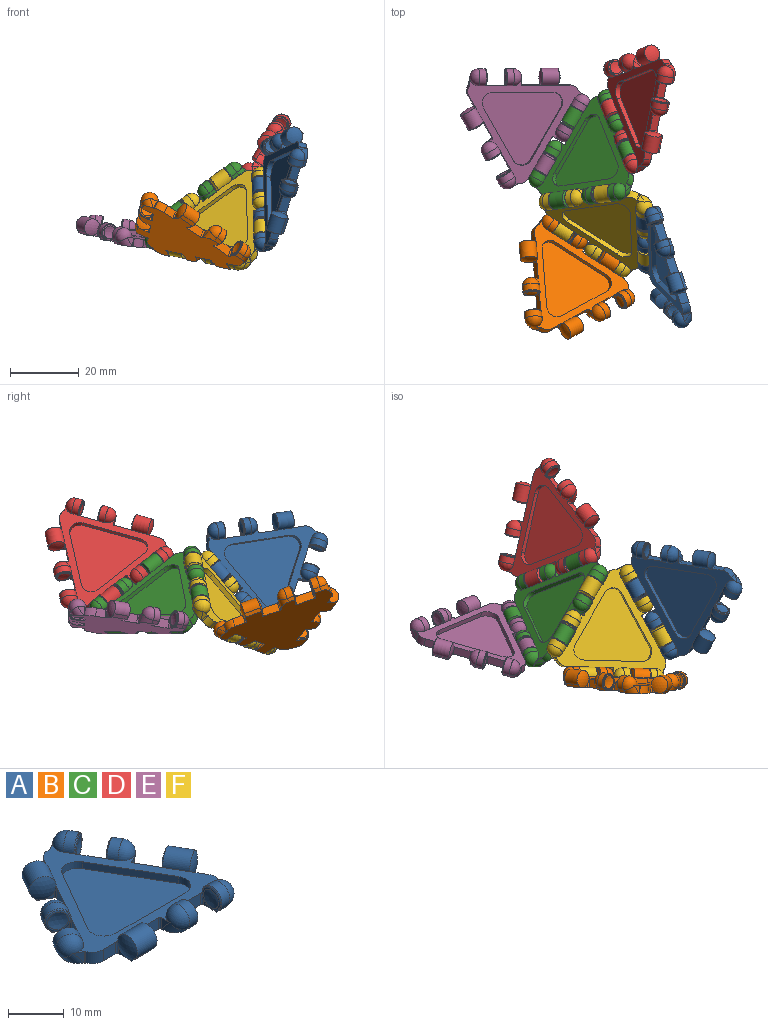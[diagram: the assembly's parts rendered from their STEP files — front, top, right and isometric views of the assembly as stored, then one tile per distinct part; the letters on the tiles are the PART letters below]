
ASSEMBLY  parts=6 mates=5
PART A: 123 faces, bbox 39.1x39.1x12.5 mm
  f0: plane 34.77x32.31mm, normal (0,0,1), area 210.3mm2, adj f1,f3,f6,f8,f9,f11,f12,f13
  f1: torus R=0.01mm, axis (1,0,0), area 24mm2, adj f0,f2,f3,f36
  f2: cylinder r=2.49mm len=4.09mm, axis (0,-0.64,0.77), area 8.6mm2, adj f1,f4,f5,f36
  f3: cylinder r=2.5mm len=5mm, axis (-1,0,0), area 19.4mm2, adj f0,f1,f4,f27
  f4: plane 2.02x0.9mm, normal (0,-0.77,-0.64), area 2.3mm2, adj f2,f3,f5,f27,f37
  f5: plane 36.71x33.87mm, normal (0,0,-1), area 668.7mm2, adj f2,f4,f7,f9,f10,f12,f14,f15
  f6: torus R=0.01mm, axis (1,0,0), area 24mm2, adj f0,f7,f8,f20
  f7: cylinder r=2.49mm len=4.09mm, axis (0,-0.64,0.77), area 8.6mm2, adj f5,f6,f20,f35
  f8: cylinder r=2.5mm len=5mm, axis (-1,0,0), area 19.4mm2, adj f0,f6,f22,f35
  f9: cylinder r=0.37mm len=2.5mm, axis (0,0,-1), area 1.2mm2, adj f0,f5,f10,f11,f16
  f10: plane 2.13x1.19mm, normal (1,0,0), area 0.7mm2, adj f5,f9,f11
  f11: sphere r=5.77mm, area 20.5mm2, adj f0,f9,f10,f30,f31
  f12: cylinder r=0.37mm len=2.5mm, axis (0,0,1), area 1.2mm2, adj f0,f5,f13,f14,f33
  f13: sphere r=5.77mm, area 20.5mm2, adj f0,f12,f14,f30,f32
  f14: plane 2.13x1.19mm, normal (-1,0,0), area 0.7mm2, adj f5,f12,f13
  f15: cylinder r=0.37mm len=2.5mm, axis (0,0,-1), area 1.5mm2, adj f0,f5,f16,f36
  f16: plane 5.03x2.5mm, normal (0,-1,0), area 12.6mm2, adj f0,f5,f9,f15
  f17: cylinder r=0.37mm len=2.5mm, axis (0,0,1), area 1.3mm2, adj f0,f5,f18,f27,f38
  f18: plane 5.39x2.5mm, normal (0,-1,0), area 13.5mm2, adj f0,f5,f17,f21
  f19: cylinder r=0.37mm len=2.5mm, axis (0,0,-1), area 0.6mm2, adj f0,f5,f20,f122
  f20: plane 2.51x2.14mm, normal (1,0,0), area 2.7mm2, adj f0,f5,f6,f7,f19
  f21: cylinder r=0.37mm len=2.5mm, axis (0,0,1), area 1.3mm2, adj f0,f5,f18,f22,f23
  f22: cone r=2.51mm half-angle=50deg, axis (1,0,0), area 4.1mm2, adj f0,f5,f8,f21,f23,f24,f34,f35
  f23: plane 1.91x1.17mm, normal (-1,0,0), area 0.7mm2, adj f5,f21,f22
  f24: torus R=2.03mm, axis (1,0,0), area 5.4mm2, adj f22,f25
  f25: sphere r=5.83mm, area 0mm2, adj f24
  f26: torus R=2.03mm, axis (-1,0,0), area 5.4mm2, adj f27,f28
  f27: cone r=2.29mm half-angle=50deg, axis (-1,0,0), area 4.1mm2, adj f0,f3,f4,f5,f17,f26,f37,f38
  f28: sphere r=5.83mm, area 11.7mm2, adj f26
  f29: plane 5x0.89mm, normal (0,-0.77,-0.64), area 5.8mm2, adj f5,f30,f31,f32
  f30: cylinder r=2.5mm len=5mm, axis (-1,0,0), area 48mm2, adj f0,f11,f13,f29
  f31: plane 1.92x0.89mm, normal (1,0,0), area 0.2mm2, adj f5,f11,f29
  f32: plane 1.92x0.89mm, normal (-1,0,0), area 0.2mm2, adj f5,f13,f29
  f33: plane 3.14x2.5mm, normal (0,-1,0), area 7.9mm2, adj f0,f5,f12,f121
  f34: plane 1.56x0.73mm, normal (-1,0,0), area 0.2mm2, adj f5,f22,f35
  f35: plane 2.02x0.9mm, normal (0,-0.77,-0.64), area 2.3mm2, adj f5,f7,f8,f22,f34
  f36: plane 2.51x2.14mm, normal (-1,0,0), area 2.7mm2, adj f0,f1,f2,f5,f15
  f37: plane 1.56x0.73mm, normal (1,0,0), area 0.2mm2, adj f4,f5,f27
  f38: plane 1.91x1.17mm, normal (1,0,0), area 0.7mm2, adj f5,f17,f27
  f39: plane 1.66x1.17mm, normal (-0.5,-0.87,0), area 0.7mm2, adj f5,f50,f60
  f40: plane 1.35x0.78mm, normal (-0.5,-0.87,0), area 0.2mm2, adj f5,f50,f72
  f41: plane 2.51x1.85mm, normal (0.5,0.87,0), area 2.7mm2, adj f0,f5,f62,f74,f75
  f42: plane 2.13x1.66mm, normal (-0.66,0.38,-0.64), area 2.3mm2, adj f5,f43,f55,f69,f70
  f43: plane 1.35x0.78mm, normal (0.5,0.87,0), area 0.2mm2, adj f5,f42,f55
  f44: plane 2.72x2.5mm, normal (-0.87,0.5,0), area 7.9mm2, adj f0,f5,f65,f120
  f45: plane 1.66x0.96mm, normal (0.5,0.87,0), area 0.2mm2, adj f5,f48,f64
  f46: plane 1.66x0.96mm, normal (-0.5,-0.87,0), area 0.2mm2, adj f5,f48,f66
  f47: cylinder r=2.5mm len=6.83mm, axis (0.5,0.87,0), area 48mm2, adj f0,f48,f64,f66
  f48: plane 4.7x3.15mm, normal (-0.66,0.38,-0.64), area 5.8mm2, adj f5,f45,f46,f47
  f49: sphere r=5.83mm, area 11.7mm2, adj f51
  f50: cone r=2.29mm half-angle=50deg, axis (0.5,0.87,0), area 4.1mm2, adj f0,f5,f39,f40,f51,f60,f72,f73
  f51: torus R=2.03mm, axis (0.5,0.87,0), area 5.4mm2, adj f49,f50
  f52: sphere r=5.83mm, area 0mm2, adj f53
  f53: torus R=2.03mm, axis (-0.5,-0.87,0), area 5.4mm2, adj f52,f55
  f54: plane 1.66x1.17mm, normal (0.5,0.87,0), area 0.7mm2, adj f5,f55,f56
  f55: cone r=2.51mm half-angle=50deg, axis (-0.5,-0.87,0), area 4.1mm2, adj f0,f5,f42,f43,f53,f54,f56,f69
  f56: cylinder r=0.37mm len=2.5mm, axis (0,0,1), area 1.3mm2, adj f0,f5,f54,f55,f59
  f57: plane 2.51x1.85mm, normal (-0.5,-0.87,0), area 2.7mm2, adj f0,f5,f58,f70,f71
  f58: cylinder r=0.37mm len=2.5mm, axis (0,0,-1), area 0.6mm2, adj f0,f5,f57,f121
  f59: plane 4.67x2.7mm, normal (-0.87,0.5,0), area 13.5mm2, adj f0,f5,f56,f60
  f60: cylinder r=0.37mm len=2.5mm, axis (0,0,1), area 1.3mm2, adj f0,f5,f39,f50,f59
  f61: plane 4.36x2.52mm, normal (-0.87,0.5,0), area 12.6mm2, adj f0,f5,f62,f68
  f62: cylinder r=0.37mm len=2.5mm, axis (0,0,-1), area 1.5mm2, adj f0,f5,f41,f61
  f63: plane 1.84x1.19mm, normal (0.5,0.87,0), area 0.7mm2, adj f5,f64,f65
  f64: sphere r=5.77mm, area 20.5mm2, adj f0,f45,f47,f63,f65
  f65: cylinder r=0.37mm len=2.5mm, axis (0,0,1), area 1.2mm2, adj f0,f5,f44,f63,f64
  f66: sphere r=5.77mm, area 20.5mm2, adj f0,f46,f47,f67,f68
  f67: plane 1.84x1.19mm, normal (-0.5,-0.87,0), area 0.7mm2, adj f5,f66,f68
  f68: cylinder r=0.37mm len=2.5mm, axis (0,0,-1), area 1.2mm2, adj f0,f5,f61,f66,f67
  f69: cylinder r=2.5mm len=5.34mm, axis (0.5,0.87,0), area 19.4mm2, adj f0,f42,f55,f71
  f70: cylinder r=2.49mm len=4.16mm, axis (-0.56,0.32,0.77), area 8.6mm2, adj f5,f42,f57,f71
  f71: torus R=0.01mm, axis (-0.5,-0.87,0), area 24mm2, adj f0,f57,f69,f70
  f72: plane 2.12x1.66mm, normal (-0.66,0.38,-0.64), area 2.3mm2, adj f5,f40,f50,f73,f74
  f73: cylinder r=2.5mm len=5.34mm, axis (0.5,0.87,0), area 19.4mm2, adj f0,f50,f72,f75
  f74: cylinder r=2.49mm len=4.71mm, axis (-0.56,0.32,0.77), area 8.6mm2, adj f5,f41,f72,f75
  f75: torus R=0.01mm, axis (-0.5,-0.87,0), area 24mm2, adj f0,f41,f73,f74
  f76: plane 1.66x1.17mm, normal (-0.5,0.87,0), area 0.7mm2, adj f5,f87,f97
  f77: plane 1.35x0.78mm, normal (-0.5,0.87,0), area 0.2mm2, adj f5,f87,f109
  f78: plane 2.51x1.85mm, normal (0.5,-0.87,0), area 2.7mm2, adj f0,f5,f99,f111,f112
  f79: plane 2.12x1.66mm, normal (0.66,0.38,-0.64), area 2.3mm2, adj f5,f80,f92,f106,f107
  f80: plane 1.35x0.78mm, normal (0.5,-0.87,0), area 0.2mm2, adj f5,f79,f92
  f81: plane 2.72x2.5mm, normal (0.87,0.5,0), area 7.9mm2, adj f0,f5,f102,f122
  f82: plane 1.66x0.96mm, normal (0.5,-0.87,0), area 0.2mm2, adj f5,f85,f101
  f83: plane 1.66x0.96mm, normal (-0.5,0.87,0), area 0.2mm2, adj f5,f85,f103
  f84: cylinder r=2.5mm len=6.83mm, axis (0.5,-0.87,0), area 48mm2, adj f0,f85,f101,f103
  f85: plane 4.7x3.15mm, normal (0.66,0.38,-0.64), area 5.8mm2, adj f5,f82,f83,f84
  f86: sphere r=5.83mm, area 11.7mm2, adj f88
  f87: cone r=2.29mm half-angle=50deg, axis (0.5,-0.87,0), area 4.1mm2, adj f0,f5,f76,f77,f88,f97,f109,f110
  f88: torus R=2.03mm, axis (0.5,-0.87,0), area 5.4mm2, adj f86,f87
  f89: sphere r=5.83mm, area 427.2mm2, adj f90
  f90: torus R=2.03mm, axis (-0.5,0.87,0), area 5.4mm2, adj f89,f92
  f91: plane 1.66x1.17mm, normal (0.5,-0.87,0), area 0.7mm2, adj f5,f92,f93
  f92: cone r=2.51mm half-angle=50deg, axis (-0.5,0.87,0), area 4.1mm2, adj f0,f5,f79,f80,f90,f91,f93,f106
  f93: cylinder r=0.37mm len=2.5mm, axis (0,0,1), area 1.3mm2, adj f0,f5,f91,f92,f96
  f94: plane 2.51x1.85mm, normal (-0.5,0.87,0), area 2.7mm2, adj f0,f5,f95,f107,f108
  f95: cylinder r=0.37mm len=2.5mm, axis (0,0,-1), area 0.6mm2, adj f0,f5,f94,f120
  f96: plane 4.67x2.7mm, normal (0.87,0.5,0), area 13.5mm2, adj f0,f5,f93,f97
  f97: cylinder r=0.37mm len=2.5mm, axis (0,0,1), area 1.3mm2, adj f0,f5,f76,f87,f96
  f98: plane 4.36x2.52mm, normal (0.87,0.5,0), area 12.6mm2, adj f0,f5,f99,f105
  f99: cylinder r=0.37mm len=2.5mm, axis (0,0,-1), area 1.5mm2, adj f0,f5,f78,f98
  f100: plane 1.84x1.19mm, normal (0.5,-0.87,0), area 0.7mm2, adj f5,f101,f102
  f101: sphere r=5.77mm, area 20.5mm2, adj f0,f82,f84,f100,f102
  f102: cylinder r=0.37mm len=2.5mm, axis (0,0,1), area 1.2mm2, adj f0,f5,f81,f100,f101
  f103: sphere r=5.77mm, area 20.5mm2, adj f0,f83,f84,f104,f105
  f104: plane 1.84x1.19mm, normal (-0.5,0.87,0), area 0.7mm2, adj f5,f103,f105
  f105: cylinder r=0.37mm len=2.5mm, axis (0,0,-1), area 1.2mm2, adj f0,f5,f98,f103,f104
  f106: cylinder r=2.5mm len=5.34mm, axis (0.5,-0.87,0), area 19.4mm2, adj f0,f79,f92,f108
  f107: cylinder r=2.49mm len=4.71mm, axis (0.56,0.32,0.77), area 8.6mm2, adj f5,f79,f94,f108
  f108: torus R=0.01mm, axis (-0.5,0.87,0), area 24mm2, adj f0,f94,f106,f107
  f109: plane 2.13x1.66mm, normal (0.66,0.38,-0.64), area 2.3mm2, adj f5,f77,f87,f110,f111
  f110: cylinder r=2.5mm len=5.34mm, axis (0.5,-0.87,0), area 19.4mm2, adj f0,f87,f109,f112
  f111: cylinder r=2.49mm len=4.16mm, axis (0.56,0.32,0.77), area 8.6mm2, adj f5,f78,f109,f112
  f112: torus R=0.01mm, axis (-0.5,0.87,0), area 24mm2, adj f0,f78,f110,f111
  f113: plane 15.31x8.84mm, normal (0.87,-0.5,0), area 26.5mm2, adj f0,f116,f117,f118
  f114: plane 17.68x1.5mm, normal (0,1,0), area 26.5mm2, adj f0,f116,f117,f119
  f115: plane 15.31x8.84mm, normal (-0.87,-0.5,0), area 26.5mm2, adj f0,f116,f118,f119
  f116: plane 23.68x21.31mm, normal (0,0,1), area 322.7mm2, adj f113,f114,f115,f117,f118,f119
  f117: cylinder r=3mm len=4.5mm, axis (0,0,1), area 9.4mm2, adj f0,f113,f114,f116
  f118: cylinder r=3mm len=5.2mm, axis (0,0,1), area 9.4mm2, adj f0,f113,f115,f116
  f119: cylinder r=3mm len=4.5mm, axis (0,0,1), area 9.4mm2, adj f0,f114,f115,f116
  f120: cylinder r=3mm len=2.88mm, axis (0,0,-1), area 8.6mm2, adj f0,f5,f44,f95
  f121: cylinder r=3mm len=2.73mm, axis (0,0,-1), area 8.6mm2, adj f0,f5,f33,f58
  f122: cylinder r=3mm len=3.24mm, axis (0,0,-1), area 8.6mm2, adj f0,f5,f19,f81
PART B: same geometry as A
PART C: same geometry as A
PART D: same geometry as A
PART E: same geometry as A
PART F: same geometry as A
PLACE A rot(axis=(-0.45,-0.52,0.72),130.9deg) t=(11.25,-28.07,-19.39)mm
PLACE B rot(axis=(0.16,0.23,0.96),151.3deg) t=(-16.25,-27.75,-50.25)mm
PLACE C rot(axis=(-0.41,0,0.91),124.4deg) t=(-4.86,6.07,-35.67)mm fixed
PLACE D rot(axis=(0.5,-0.07,-0.87),171.5deg) t=(1.97,26.32,-28.35)mm
PLACE E rot(axis=(0.14,0.08,0.99),60.7deg) t=(-24.34,7.06,-47.59)mm
PLACE F rot(axis=(0.84,-0.09,-0.54),64.3deg) t=(-12.19,-22.14,-48.9)mm
MATE revolute F.f53 <-> C.f53  axis (0.8,0.11,0.58) through (-6.62,-9.62,-26.49)mm
MATE revolute D.f88 <-> C.f27  axis (-0.3,0.75,-0.58) through (-7.59,16.14,-39.05)mm
MATE revolute E.f27 <-> C.f88  axis (0.5,0.87,0) through (-16.66,14.61,-45.53)mm
MATE revolute B.f30 <-> F.f27  axis (0.83,-0.53,-0.18) through (-5.34,-30.68,-51.27)mm
MATE revolute A.f88 <-> F.f90  axis (-0.03,0.64,0.76) through (2.82,-15.47,-28.31)mm
